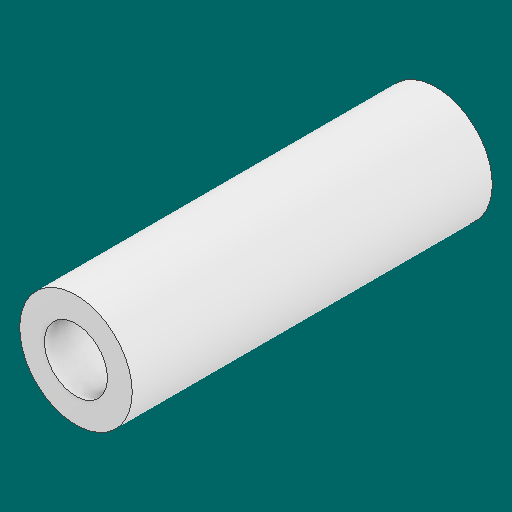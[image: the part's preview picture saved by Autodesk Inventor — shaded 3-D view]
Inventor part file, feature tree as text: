
AUTODESK INVENTOR PART (.ipt)
format: ipt  version: 2023.1 (Build 271208000, 208)  size: 97,280 bytes
history: native  units: in
note: dims shown in document units (in); Inventor stores cm internally (conversion verified against a paired STEP export)
features: other x3, sketch x1
ambient origin geometry x8: Origin, YZ Plane, XZ Plane, XY Plane, X Axis, Y Axis, Z Axis, Center Point
bodies: Solid1 (feature_tree)
feature tree (4):
  other  "1.2inSpacer_MIR.ipt"
  other  "Solid1::1.2inSpacer_MIR.ipt"
  other  "TaggingFeature1"
  sketch  "Sketch1"  dims[d0=0.3937in]
